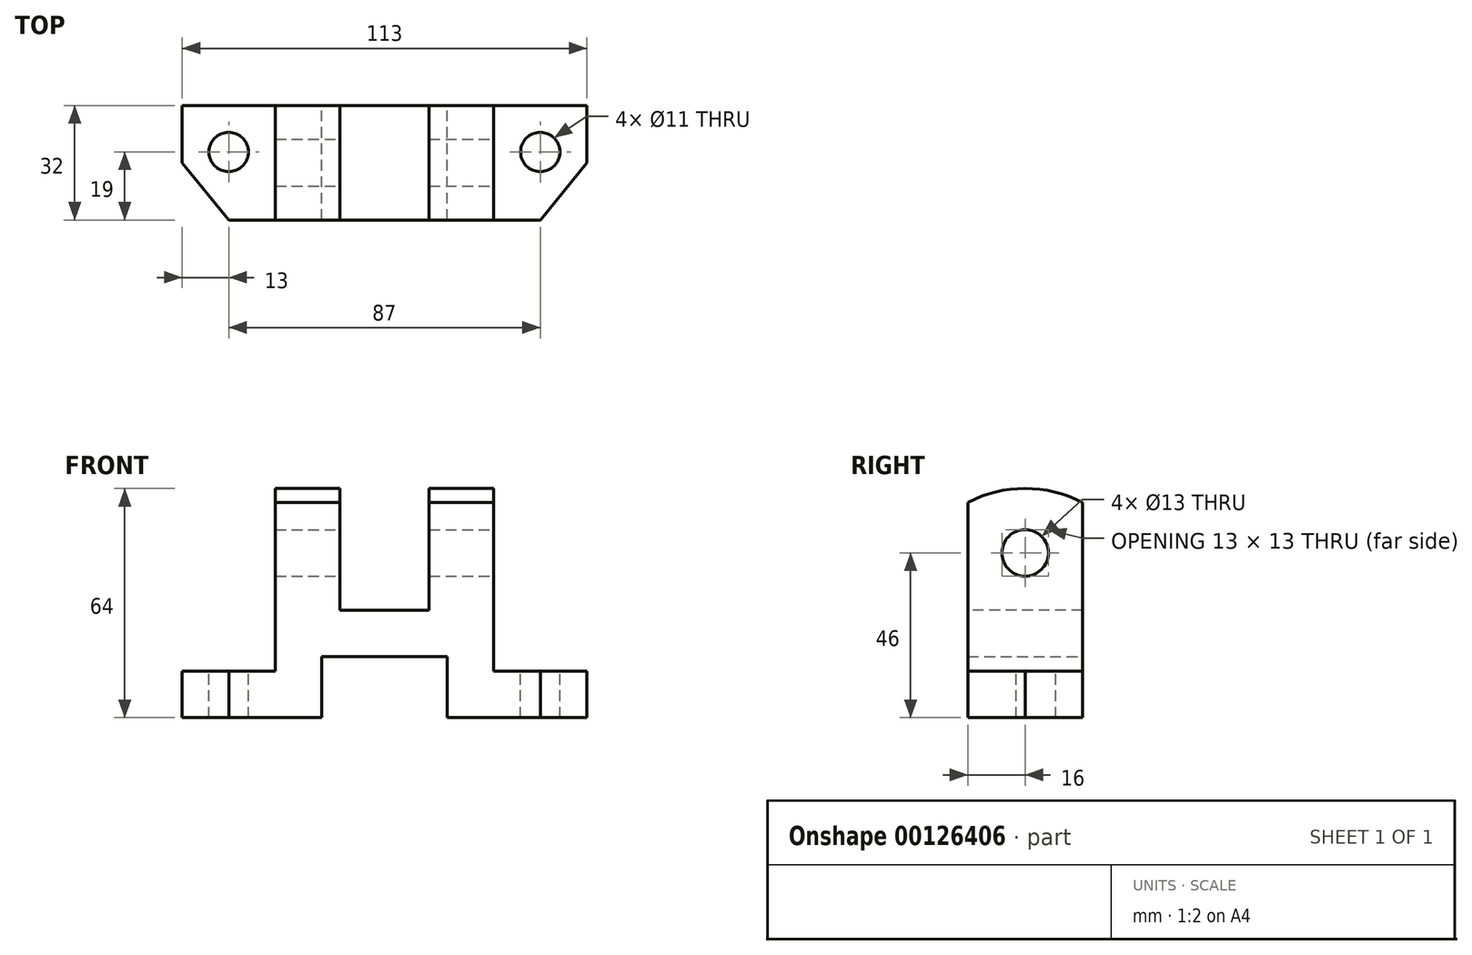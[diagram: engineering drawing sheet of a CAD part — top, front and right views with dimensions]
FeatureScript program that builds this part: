
annotation { "Feature Type Name" : "Feature", "Feature Type Description" : "" }
export const myFeature = defineFeature(function(context is Context, id is Id, definition is map)
    precondition{}
    {
        {
            var Q0;
            Q0=qCreatedBy(makeId("Right.planeOp"),FACE);
            var sketch = newSketch(context, id + "F0", { "sketchPlane" : qUnion([Q0])});
            skLineSegment(sketch, "E0.bottom", {"start": v(0, 0) * mm, "end": v(32, 0) * mm});
            skLineSegment(sketch, "E0.top", {"start": v(0, 13) * mm, "end": v(32, 13) * mm});
            skLineSegment(sketch, "E0.left", {"start": v(0, 0) * mm, "end": v(0, 13) * mm});
            skLineSegment(sketch, "E0.right", {"start": v(32, 0) * mm, "end": v(32, 13) * mm});
            skLineSegment(sketch, "E1", {"start": v(0, 13) * mm, "end": v(0, 60.13) * mm});
            skLineSegment(sketch, "E2", {"start": v(32, 13) * mm, "end": v(32, 60.13) * mm});
            skArc(sketch, "E3", {"start": v(32, 60.13) * mm, "mid": v(16, 64) * mm, "end": v(0, 60.13) * mm});
            skPoint(sketch, "E4", {"position": v(16, 64) * mm});
            skSolve(sketch);
        }
        {
            var Q0;
            Q0=qSketchRegion(id+"F0",true);
            extrude(context, id + "F1", {"entities" : qUnion([Q0]), "depth" : 113 * mm});
        }
        {
            var Q0;
            Q0=makeQuery(id+"F1.opExtrude","SWEPT_FACE",FACE,{"disambiguationData":[OSD([sQuery(id+"F0.wireOp",EDGE,"E0.bottom")])]});
            var sketch = newSketch(context, id + "F2", { "sketchPlane" : qUnion([Q0])});
            skLineSegment(sketch, "E5.bottom", {"start": v(39, 0) * mm, "end": v(74, 0) * mm});
            skLineSegment(sketch, "E5.top", {"start": v(39, -32) * mm, "end": v(74, -32) * mm});
            skLineSegment(sketch, "E5.left", {"start": v(39, 0) * mm, "end": v(39, -32) * mm});
            skLineSegment(sketch, "E5.right", {"start": v(74, 0) * mm, "end": v(74, -32) * mm});
            skSolve(sketch);
        }
        {
            var Q0;
            Q0=makeQuery(id+"F2.imprint","IMPRINT",FACE,{"disambiguationData":[TD([[makeQuery(id+"F2.imprint","IMPRINT",EDGE,{"derivedFrom":sQuery(id+"F2.wireOp",EDGE,"E5.bottom")}),1.0]])]});
            extrude(context, id + "F3", {"entities" : qUnion([Q0]), "operationType" : NewBodyOperationType.REMOVE, "oppositeDirection" : true, "depth" : 17 * mm});
        }
        {
            var Q0;
            Q0=makeQuery(id+"F1.opExtrude","SWEPT_FACE",FACE,{"disambiguationData":[OSD([sQuery(id+"F0.wireOp",EDGE,"E0.left"),sQuery(id+"F0.wireOp",EDGE,"E1")])]});
            var sketch = newSketch(context, id + "F4", { "sketchPlane" : qUnion([Q0])});
            skLineSegment(sketch, "E6", {"start": v(113, 0) * mm, "end": v(113, 13) * mm});
            skLineSegment(sketch, "E7", {"start": v(113, 13) * mm, "end": v(87, 13) * mm});
            skLineSegment(sketch, "E8", {"start": v(87, 13) * mm, "end": v(87, 78.94) * mm});
            skLineSegment(sketch, "E9", {"start": v(87, 78.94) * mm, "end": v(74, 78.94) * mm});
            skLineSegment(sketch, "E10", {"start": v(69, 30) * mm, "end": v(44, 30) * mm});
            skLineSegment(sketch, "E11", {"start": v(44, 30) * mm, "end": v(44, 78.94) * mm});
            skLineSegment(sketch, "E12", {"start": v(44, 78.94) * mm, "end": v(26, 78.94) * mm});
            skLineSegment(sketch, "E13", {"start": v(26, 78.94) * mm, "end": v(26, 13) * mm});
            skLineSegment(sketch, "E14", {"start": v(0, 13) * mm, "end": v(0, 0) * mm});
            skLineSegment(sketch, "E15", {"start": v(44, 78.94) * mm, "end": v(74, 78.94) * mm});
            skLineSegment(sketch, "E16", {"start": v(87, 78.94) * mm, "end": v(113, 78.94) * mm});
            skLineSegment(sketch, "E17", {"start": v(113, 78.94) * mm, "end": v(113, 13) * mm});
            skLineSegment(sketch, "E18", {"start": v(26, 78.94) * mm, "end": v(0, 78.94) * mm});
            skLineSegment(sketch, "E19", {"start": v(0, 78.94) * mm, "end": v(0, 13) * mm});
            skPoint(sketch, "E20", {"position": v(56.5, 30) * mm});
            skPoint(sketch, "E21", {"position": v(56.5, 17) * mm});
            skLineSegment(sketch, "E22", {"start": v(56.5, 30) * mm, "end": v(56.5, 17) * mm, "construction": true});
            skLineSegment(sketch, "E23", {"start": v(26, 13) * mm, "end": v(0, 13) * mm});
            skLineSegment(sketch, "E24", {"start": v(69, 30) * mm, "end": v(69, 78.94) * mm});
            skSolve(sketch);
        }
        {
            var Q0;
            {var subQ0=sQuery(id+"F4.wireOp",EDGE,"E10");Q0=makeQuery(id+"F4.imprint","IMPRINT",FACE,{"disambiguationData":[TD([[makeQuery(id+"F4.imprint","IMPRINT",EDGE,{"derivedFrom":subQ0}),-1.0]])]});}
            var Q1;
            {var subQ0=sQuery(id+"F4.wireOp",EDGE,"E15");var subQ5=sQuery(id+"F4.wireOp",EDGE,"E24");var subQ6=makeQuery(id+"F4.imprint","INTERSECT",VERTEX,{"derivedFrom":[subQ0,subQ5]});Q1=makeQuery(id+"F4.imprint","IMPRINT",FACE,{"disambiguationData":[TD([[makeQuery(id+"F4.imprint","IMPRINT",EDGE,{"disambiguationData":[TD([[subQ6,1.0]])],"derivedFrom":subQ0}),-1.0]])]});}
            var Q2;
            {var subQ0=sQuery(id+"F4.wireOp",EDGE,"E7");Q2=makeQuery(id+"F4.imprint","IMPRINT",FACE,{"disambiguationData":[TD([[makeQuery(id+"F4.imprint","IMPRINT",EDGE,{"derivedFrom":subQ0}),-1.0]])]});}
            var Q3;
            {var subQ0=sQuery(id+"F4.wireOp",EDGE,"E16");Q3=makeQuery(id+"F4.imprint","IMPRINT",FACE,{"disambiguationData":[TD([[makeQuery(id+"F4.imprint","IMPRINT",EDGE,{"derivedFrom":subQ0}),-1.0]])]});}
            var Q4;
            {var subQ0=sQuery(id+"F4.wireOp",EDGE,"E18");Q4=makeQuery(id+"F4.imprint","IMPRINT",FACE,{"disambiguationData":[TD([[makeQuery(id+"F4.imprint","IMPRINT",EDGE,{"derivedFrom":subQ0}),1.0]])]});}
            var Q5;
            {var subQ0=sQuery(id+"F4.wireOp",EDGE,"E23");Q5=makeQuery(id+"F4.imprint","IMPRINT",FACE,{"disambiguationData":[TD([[makeQuery(id+"F4.imprint","IMPRINT",EDGE,{"derivedFrom":subQ0}),-1.0]])]});}
            extrude(context, id + "F5", {"entities" : qUnion([Q0, Q1, Q2, Q3, Q4, Q5]), "operationType" : NewBodyOperationType.REMOVE, "endBound" : BoundingType.THROUGH_ALL, "oppositeDirection" : true, "depth" : 25 * mm});
        }
        {
            var Q0;
            Q0=makeQuery(id+"F5.boolean.opBoolean","COPY",FACE,{"derivedFrom":makeQuery(id+"F5.opExtrude","SWEPT_FACE",FACE,{"disambiguationData":[OSD([sQuery(id+"F4.wireOp",EDGE,"E7")])]})});
            var sketch = newSketch(context, id + "F6", { "sketchPlane" : qUnion([Q0])});
            skLineSegment(sketch, "E25.bottom", {"start": v(87, 32) * mm, "end": v(113, 32) * mm});
            skLineSegment(sketch, "E25.top", {"start": v(87, 0) * mm, "end": v(100, 0) * mm});
            skLineSegment(sketch, "E25.left", {"start": v(87, 32) * mm, "end": v(87, 0) * mm});
            skLineSegment(sketch, "E25.right", {"start": v(113, 32) * mm, "end": v(113, 16) * mm});
            skLineSegment(sketch, "E26", {"start": v(100, 0) * mm, "end": v(113, 16) * mm});
            skCircle(sketch, "E27", {"center": v(100, 19) * mm, "radius": 5.5 * mm});
            skPoint(sketch, "E27.centerSnap0", {"position": v(100, 32) * mm});
            skSolve(sketch);
        }
        {
            var Q0;
            {var subQ0=sQuery(id+"F6.wireOp",EDGE,"E26");Q0=makeQuery(id+"F6.imprint","IMPRINT",FACE,{"disambiguationData":[TD([[makeQuery(id+"F6.imprint","IMPRINT",EDGE,{"derivedFrom":subQ0}),-1.0]])]});}
            var Q1;
            Q1=makeQuery(id+"F6.imprint","IMPRINT",FACE,{"disambiguationData":[TD([[makeQuery(id+"F6.imprint","IMPRINT",EDGE,{"derivedFrom":sQuery(id+"F6.wireOp",EDGE,"E27")}),1.0]])]});
            extrude(context, id + "F7", {"entities" : qUnion([Q0, Q1]), "operationType" : NewBodyOperationType.REMOVE, "endBound" : BoundingType.THROUGH_ALL, "oppositeDirection" : true, "depth" : 25 * mm});
        }
        {
            var Q0;
            Q0=makeQuery(id+"F5.boolean.opBoolean","COPY",FACE,{"derivedFrom":makeQuery(id+"F5.opExtrude","SWEPT_FACE",FACE,{"disambiguationData":[OSD([sQuery(id+"F4.wireOp",EDGE,"E23")])]})});
            var sketch = newSketch(context, id + "F8", { "sketchPlane" : qUnion([Q0])});
            skLineSegment(sketch, "E28.bottom", {"start": v(0, 0) * mm, "end": v(26, 0) * mm});
            skLineSegment(sketch, "E28.top", {"start": v(0, 32) * mm, "end": v(26, 32) * mm});
            skLineSegment(sketch, "E28.left", {"start": v(0, 0) * mm, "end": v(0, 32) * mm});
            skLineSegment(sketch, "E28.right", {"start": v(26, 0) * mm, "end": v(26, 32) * mm});
            skLineSegment(sketch, "E29", {"start": v(0, 16) * mm, "end": v(13, 0) * mm});
            skCircle(sketch, "E30", {"center": v(13, 19) * mm, "radius": 5.5 * mm});
            skPoint(sketch, "E30.centerSnap0", {"position": v(13, 32) * mm});
            skSolve(sketch);
        }
        {
            var Q0;
            Q0=makeQuery(id+"F8.imprint","IMPRINT",FACE,{"disambiguationData":[TD([[makeQuery(id+"F8.imprint","IMPRINT",EDGE,{"derivedFrom":sQuery(id+"F8.wireOp",EDGE,"E30")}),1.0]])]});
            var Q1;
            {var subQ3=sQuery(id+"F8.wireOp",EDGE,"E29");Q1=makeQuery(id+"F8.imprint","IMPRINT",FACE,{"disambiguationData":[TD([[makeQuery(id+"F8.imprint","IMPRINT",EDGE,{"derivedFrom":subQ3}),-1.0]])]});}
            extrude(context, id + "F9", {"entities" : qUnion([Q0, Q1]), "operationType" : NewBodyOperationType.REMOVE, "endBound" : BoundingType.THROUGH_ALL, "oppositeDirection" : true, "depth" : 25 * mm});
        }
        {
            var Q0;
            Q0=makeQuery(id+"F5.boolean.opBoolean","COPY",FACE,{"derivedFrom":makeQuery(id+"F5.opExtrude","SWEPT_FACE",FACE,{"disambiguationData":[OSD([sQuery(id+"F4.wireOp",EDGE,"E8")])]})});
            var sketch = newSketch(context, id + "F10", { "sketchPlane" : qUnion([Q0])});
            skCircle(sketch, "E31", {"center": v(16, 46) * mm, "radius": 6.5 * mm});
            skPoint(sketch, "E31.centerSnap0", {"position": v(16, 64) * mm});
            skSolve(sketch);
        }
        {
            var Q0;
            Q0=makeQuery(id+"F10.imprint","IMPRINT",FACE,{"disambiguationData":[TD([[makeQuery(id+"F10.imprint","IMPRINT",EDGE,{"derivedFrom":sQuery(id+"F10.wireOp",EDGE,"E31")}),1.0]])]});
            extrude(context, id + "F11", {"entities" : qUnion([Q0]), "operationType" : NewBodyOperationType.REMOVE, "endBound" : BoundingType.THROUGH_ALL, "oppositeDirection" : true, "depth" : 25 * mm});
        }
    });
